# Revit family: 33-50-011-DN80-300
name_source: partatom
category: Pipe Accessories
units: mm (PartAtom-declared; Revit-internal decimal feet)

## family parameters
Always vertical = No
Cut with Voids When Loaded = No
Part Type = Valve - Breaks Into
Round Connector Dimension = Use Diameter
Shared = No
Work Plane-Based = No

## types (7) — shared parameters
33-080-50-017 = DN080_PN16
33-100-50-017 = DN100_PN16
33-125-50-017 = DN125_PN16
33-150-50-017 = DN150_PN16
33-200-50-017 = DN200_PN16
33-250-50-017 = DN250_PN16
33-300-50-017 = DN300_PN16
Body_Wallthickness = 15 mm  [stored 0.0492126 ft]
Description_ = AVK GATE VALVE, BLS SOCKET/SPIGOT ENDS
Ftc = 4 mm  [stored 0.0131234 ft]
Name_Height_reference = 10 mm  [stored 0.0328084 ft]
Rib_Height_Reference_3 = 100 mm
Rib_Thickness = 18 mm  [stored 0.0590551 ft]
Search_table = 33-50-011-DN80-300
URL product pages = https://www.avkvalves.com
zero-valued in all types: Bottom_Reference

## per-type parameters (varying)
- DN080_PN16: At=70 mm; Body_Height=132 mm; Body_depth=140 mm; Body_width=75 mm; Body_width_ref=150 mm; Bonnet_Flange_Depth=171 mm; Bonnet_Flange_Width=90 mm; Bonnet_Flange_cut=8 mm  [stored 0.0262467 ft]; Bonnet_Flange_thickness=15 mm  [stored 0.0492126 ft]; Bonnet_Height=50 mm  [stored 0.164042 ft]; Bonnet_Reference_height=122 mm; Bonnet_Thickness=77 mm; Bt=77 mm; Bt_2=69 mm; CL _Thickness=27 mm  [stored 0.0885827 ft]; CL_Height=75 mm; Cut_Reference=860 mm; D=49 mm  [stored 0.160761 ft]; D2=34 mm  [stored 0.111549 ft]; D_ref=50 mm  [stored 0.164042 ft]; D_ref_2=46 mm  [stored 0.150919 ft]; Dd=98 mm; Dd_2=150 mm; Dd_2_ref=66 mm; F=9 mm  [stored 0.0295276 ft]; F1=10 mm  [stored 0.0328084 ft]; F1_ref=20 mm  [stored 0.0656168 ft]; Fillet_Thickness=6 mm  [stored 0.019685 ft]; Flange_OR=100 mm; Flange_Thickness=54 mm; Flange_Thickness_cut=30 mm  [stored 0.0984252 ft]; Ftc_reference_height=100 mm; H=297 mm; H1=263 mm; H3=372 mm; H3_ref=75 mm; Horizontal_Flange_width=150 mm; ID=40 mm  [stored 0.131234 ft]; L=430 mm; L1=85 mm; L2=140 mm; L_Dia=80 mm; L_ref=172 mm; Name_Reference=90 mm; Name_Width=38 mm  [stored 0.124672 ft]; Neck_H=56 mm; Neck_T=25 mm  [stored 0.082021 ft]; Neck_T2=23 mm  [stored 0.0754593 ft]; Nominal Diameter (DN)=80 mm; R1tv=1000 mm; R2f=15 mm  [stored 0.0492126 ft]; RF_Dia=66 mm; Rf=250 mm; Rib_Height_Reference_1=120 mm; Rib_Height_Reference_2=110 mm; Rib_Height_Reference_4=85 mm; Rib_Width_1=38 mm  [stored 0.124672 ft]; Rib_Width_2=38 mm  [stored 0.124672 ft]; Rib_Width_3=38 mm  [stored 0.124672 ft]; Rib_depth_1=38 mm  [stored 0.124672 ft]; Rib_depth_2=38 mm  [stored 0.124672 ft]; Rib_depth_3=38 mm  [stored 0.124672 ft]; Rt=333 mm; S=3 mm  [stored 0.00984252 ft]
- DN100_PN16: At=83 mm; Body_Height=148 mm; Body_depth=166 mm; Body_width=80 mm; Body_width_ref=160 mm; Bonnet_Flange_Depth=192 mm; Bonnet_Flange_Width=100 mm; Bonnet_Flange_cut=8 mm  [stored 0.0262467 ft]; Bonnet_Flange_thickness=15 mm  [stored 0.0492126 ft]; Bonnet_Height=55 mm; Bonnet_Reference_height=138 mm; Bonnet_Thickness=82 mm; Bt=82 mm; Bt_2=74 mm; CL _Thickness=29 mm  [stored 0.0951444 ft]; CL_Height=88 mm; Cut_Reference=920 mm; D=59 mm; D2=38 mm  [stored 0.124672 ft]; D_ref=60 mm; D_ref_2=56 mm; Dd=118 mm; Dd_2=171 mm; Dd_2_ref=77 mm; F=10 mm  [stored 0.0328084 ft]; F1=11 mm  [stored 0.0360892 ft]; F1_ref=22 mm  [stored 0.0721785 ft]; Fillet_Thickness=6 mm  [stored 0.019685 ft]; Flange_OR=110 mm; Flange_Thickness=54 mm; Flange_Thickness_cut=30 mm  [stored 0.0984252 ft]; Ftc_reference_height=110 mm; H=334 mm; H1=296 mm; H3=420 mm; H3_ref=86 mm; Horizontal_Flange_width=172 mm; ID=50 mm  [stored 0.164042 ft]; L=460 mm; L1=86 mm; L2=150 mm; L_Dia=100 mm; L_ref=184 mm; Name_Reference=101 mm; Name_Width=40 mm  [stored 0.131234 ft]; Neck_H=60 mm; Neck_T=27 mm  [stored 0.0885827 ft]; Neck_T2=25 mm  [stored 0.082021 ft]; Nominal Diameter (DN)=100 mm; R1tv=1100 mm; R2f=15 mm  [stored 0.0492126 ft]; RF_Dia=78 mm; Rf=287 mm; Rib_Height_Reference_1=120 mm; Rib_Height_Reference_2=110 mm; Rib_Height_Reference_4=90 mm; Rib_Width_1=40 mm  [stored 0.131234 ft]; Rib_Width_2=40 mm  [stored 0.131234 ft]; Rib_Width_3=40 mm  [stored 0.131234 ft]; Rib_depth_1=40 mm  [stored 0.131234 ft]; Rib_depth_2=40 mm  [stored 0.131234 ft]; Rib_depth_3=40 mm  [stored 0.131234 ft]; Rt=367 mm; S=4 mm  [stored 0.0131234 ft]
- DN125_PN16: At=100 mm; Body_Height=160 mm; Body_depth=200 mm; Body_width=90 mm; Body_width_ref=180 mm; Bonnet_Flange_Depth=220 mm; Bonnet_Flange_Width=90 mm; Bonnet_Flange_cut=8 mm  [stored 0.0262467 ft]; Bonnet_Flange_thickness=15 mm  [stored 0.0492126 ft]; Bonnet_Height=63 mm; Bonnet_Reference_height=150 mm; Bonnet_Thickness=92 mm; Bt=92 mm; Bt_2=84 mm; CL _Thickness=34 mm  [stored 0.111549 ft]; CL_Height=105 mm; Cut_Reference=960 mm; D=72 mm; D2=38 mm  [stored 0.124672 ft]; D_ref=73 mm; D_ref_2=69 mm; Dd=144 mm; Dd_2=199 mm; Dd_2_ref=91 mm; F=10 mm  [stored 0.0328084 ft]; F1=11 mm  [stored 0.0360892 ft]; F1_ref=22 mm  [stored 0.0721785 ft]; Fillet_Thickness=6 mm  [stored 0.019685 ft]; Flange_OR=125 mm; Flange_Thickness=54 mm; Flange_Thickness_cut=31 mm  [stored 0.101706 ft]; Ftc_reference_height=125 mm; H=375 mm; H1=337 mm; H3=475 mm; H3_ref=100 mm; Horizontal_Flange_width=200 mm; ID=63 mm; L=480 mm; L1=87 mm; L2=165 mm; L_Dia=125 mm; L_ref=192 mm; Name_Reference=114 mm; Name_Width=45 mm  [stored 0.147638 ft]; Neck_H=72 mm; Neck_T=32 mm  [stored 0.104987 ft]; Neck_T2=30 mm  [stored 0.0984252 ft]; Nominal Diameter (DN)=125 mm; R1tv=1250 mm; R2f=15 mm  [stored 0.0492126 ft]; RF_Dia=92 mm; Rf=333 mm; Rib_Height_Reference_1=120 mm; Rib_Height_Reference_2=110 mm; Rib_Height_Reference_4=120 mm; Rib_Width_1=45 mm  [stored 0.147638 ft]; Rib_Width_2=45 mm  [stored 0.147638 ft]; Rib_Width_3=45 mm  [stored 0.147638 ft]; Rib_depth_1=45 mm  [stored 0.147638 ft]; Rib_depth_2=45 mm  [stored 0.147638 ft]; Rib_depth_3=45 mm  [stored 0.147638 ft]; Rt=417 mm; S=5 mm  [stored 0.0164042 ft]
- DN150_PN16: At=121 mm; Body_Height=215 mm; Body_depth=242 mm; Body_width=95 mm; Body_width_ref=190 mm; Bonnet_Flange_Depth=272 mm; Bonnet_Flange_Width=130 mm; Bonnet_Flange_cut=8 mm  [stored 0.0262467 ft]; Bonnet_Flange_thickness=15 mm  [stored 0.0492126 ft]; Bonnet_Height=71 mm; Bonnet_Reference_height=205 mm; Bonnet_Thickness=97 mm; Bt=97 mm; Bt_2=89 mm; CL _Thickness=34 mm  [stored 0.111549 ft]; CL_Height=126 mm; Cut_Reference=1100 mm; D=85 mm; D2=38 mm  [stored 0.124672 ft]; D_ref=85 mm; D_ref_2=82 mm; Dd=170 mm; Dd_2=228 mm; Dd_2_ref=105 mm; F=10 mm  [stored 0.0328084 ft]; F1=11 mm  [stored 0.0360892 ft]; F1_ref=22 mm  [stored 0.0721785 ft]; Fillet_Thickness=12 mm  [stored 0.0393701 ft]; Flange_OR=142 mm; Flange_Thickness=54 mm; Flange_Thickness_cut=34 mm  [stored 0.111549 ft]; Ftc_reference_height=142 mm; H=448 mm; H1=410 mm; H3=562 mm; H3_ref=114 mm; Horizontal_Flange_width=228 mm; ID=75 mm; L=550 mm; L1=96 mm; L2=175 mm; L_Dia=150 mm; L_ref=220 mm; Name_Reference=143 mm; Name_Width=48 mm  [stored 0.15748 ft]; Neck_H=69 mm; Neck_T=32 mm  [stored 0.104987 ft]; Neck_T2=30 mm  [stored 0.0984252 ft]; Nominal Diameter (DN)=150 mm; R1tv=1420 mm; R2f=30 mm  [stored 0.0984252 ft]; RF_Dia=106 mm; Rf=380 mm; Rib_Height_Reference_1=120 mm; Rib_Height_Reference_2=110 mm; Rib_Height_Reference_4=150 mm; Rib_Width_1=48 mm  [stored 0.15748 ft]; Rib_Width_2=48 mm  [stored 0.15748 ft]; Rib_Width_3=48 mm  [stored 0.15748 ft]; Rib_depth_1=48 mm  [stored 0.15748 ft]; Rib_depth_2=48 mm  [stored 0.15748 ft]; Rib_depth_3=48 mm  [stored 0.15748 ft]; Rt=473 mm; S=5 mm  [stored 0.0164042 ft]
- DN200_PN16: At=165 mm; Body_Height=270 mm; Body_depth=330 mm; Body_width=108 mm; Body_width_ref=216 mm; Bonnet_Flange_Depth=332 mm; Bonnet_Flange_Width=140 mm; Bonnet_Flange_cut=13 mm; Bonnet_Flange_thickness=25 mm  [stored 0.082021 ft]; Bonnet_Height=85 mm; Bonnet_Reference_height=260 mm; Bonnet_Thickness=110 mm; Bt=110 mm; Bt_2=102 mm; CL _Thickness=34 mm  [stored 0.111549 ft]; CL_Height=170 mm; Cut_Reference=1160 mm; D=111 mm; D2=42 mm  [stored 0.137795 ft]; D_ref=110 mm; D_ref_2=108 mm; Dd=222 mm; Dd_2=285 mm; Dd_2_ref=134 mm; F=12 mm  [stored 0.0393701 ft]; F1=14 mm  [stored 0.0459318 ft]; F1_ref=28 mm  [stored 0.0918635 ft]; Fillet_Thickness=24 mm  [stored 0.0787402 ft]; Flange_OR=170 mm; Flange_Thickness=72 mm; Flange_Thickness_cut=35 mm  [stored 0.114829 ft]; Ftc_reference_height=170 mm; H=562 mm; H1=520 mm; H3=705 mm; H3_ref=143 mm; Horizontal_Flange_width=286 mm; ID=100 mm; L=580 mm; L1=110 mm; L2=200 mm; L_Dia=200 mm; L_ref=232 mm; Name_Reference=183 mm; Name_Width=54 mm; Neck_H=80 mm; Neck_T=32 mm  [stored 0.104987 ft]; Neck_T2=30 mm  [stored 0.0984252 ft]; Nominal Diameter (DN)=200 mm; R1tv=1700 mm; R2f=60 mm; RF_Dia=133 mm; Rf=477 mm; Rib_Height_Reference_1=120 mm; Rib_Height_Reference_2=110 mm; Rib_Height_Reference_4=180 mm; Rib_Width_1=54 mm; Rib_Width_2=54 mm; Rib_Width_3=54 mm; Rib_depth_1=54 mm; Rib_depth_2=54 mm; Rib_depth_3=54 mm; Rt=567 mm; S=6 mm  [stored 0.019685 ft]
- DN250_PN16: At=196 mm; Body_Height=320 mm; Body_depth=392 mm; Body_width=132 mm; Body_width_ref=264 mm; Bonnet_Flange_Depth=422 mm; Bonnet_Flange_Width=175 mm; Bonnet_Flange_cut=13 mm; Bonnet_Flange_thickness=25 mm  [stored 0.082021 ft]; Bonnet_Height=100 mm; Bonnet_Reference_height=310 mm; Bonnet_Thickness=135 mm; Bt=135 mm; Bt_2=126 mm; CL _Thickness=46 mm  [stored 0.150919 ft]; CL_Height=201 mm; Cut_Reference=1240 mm; D=137 mm; D2=47 mm  [stored 0.154199 ft]; D_ref=135 mm; D_ref_2=134 mm; Dd=274 mm; Dd_2=345 mm; Dd_2_ref=164 mm; F=14 mm  [stored 0.0459318 ft]; F1=16 mm  [stored 0.0524934 ft]; F1_ref=31 mm  [stored 0.101706 ft]; Fillet_Thickness=24 mm  [stored 0.0787402 ft]; Flange_OR=200 mm; Flange_Thickness=79 mm; Flange_Thickness_cut=38 mm  [stored 0.124672 ft]; Ftc_reference_height=200 mm; H=664 mm; H1=617 mm; H3=837 mm; H3_ref=173 mm; Horizontal_Flange_width=346 mm; ID=125 mm; L=620 mm; L1=131 mm; L2=200 mm; L_Dia=250 mm; L_ref=248 mm; Name_Reference=200 mm; Name_Width=66 mm; Neck_H=96 mm; Neck_T=44 mm  [stored 0.144357 ft]; Neck_T2=42 mm  [stored 0.137795 ft]; Nominal Diameter (DN)=250 mm; R1tv=2000 mm; R2f=60 mm; RF_Dia=160 mm; Rf=577 mm; Rib_Height_Reference_1=90 mm; Rib_Height_Reference_2=110 mm; Rib_Height_Reference_4=250 mm; Rib_Width_1=150 mm; Rib_Width_2=150 mm; Rib_Width_3=66 mm; Rib_depth_1=422 mm; Rib_depth_2=66 mm; Rib_depth_3=66 mm; Rt=667 mm; S=6 mm  [stored 0.019685 ft]
- DN300_PN16: At=209 mm; Body_Height=370 mm; Body_depth=418 mm; Body_width=160 mm; Body_width_ref=320 mm; Bonnet_Flange_Depth=448 mm; Bonnet_Flange_Width=200 mm; Bonnet_Flange_cut=18 mm  [stored 0.0590551 ft]; Bonnet_Flange_thickness=35 mm  [stored 0.114829 ft]; Bonnet_Height=114 mm; Bonnet_Reference_height=360 mm; Bonnet_Thickness=163 mm; Bt=163 mm; Bt_2=154 mm; CL _Thickness=60 mm; CL_Height=214 mm; Cut_Reference=1380 mm; D=163 mm; D2=47 mm  [stored 0.154199 ft]; D_ref=160 mm; D_ref_2=160 mm; Dd=326 mm; Dd_2=398 mm; Dd_2_ref=190 mm; F=14 mm  [stored 0.0459318 ft]; F1=16 mm  [stored 0.0524934 ft]; F1_ref=31 mm  [stored 0.101706 ft]; Fillet_Thickness=24 mm  [stored 0.0787402 ft]; Flange_OR=228 mm; Flange_Thickness=90 mm; Flange_Thickness_cut=39 mm  [stored 0.127953 ft]; Ftc_reference_height=228 mm; H=740 mm; H1=693 mm; H3=939 mm; H3_ref=199 mm; Horizontal_Flange_width=398 mm; ID=150 mm; L=690 mm; L1=129 mm; L2=200 mm; L_Dia=300 mm; L_ref=276 mm; Name_Reference=300 mm; Name_Width=80 mm; Neck_H=109 mm; Neck_T=58 mm; Neck_T2=56 mm; Nominal Diameter (DN)=300 mm; R1tv=2275 mm; R2f=60 mm; RF_Dia=185 mm; Rf=663 mm; Rib_Height_Reference_1=113 mm; Rib_Height_Reference_2=285 mm; Rib_Height_Reference_4=325 mm; Rib_Width_1=210 mm; Rib_Width_2=210 mm; Rib_Width_3=80 mm; Rib_depth_1=455 mm; Rib_depth_2=455 mm; Rib_depth_3=80 mm; Rt=758 mm; S=7 mm

note: [stored X ft] marks values corroborated as IEEE doubles in the binary element streams (Revit-internal decimal feet)

## geometry (parser evidence)
native form markers: Extrusion x1, Sweep x2
no freeform markers — native parametric forms only
